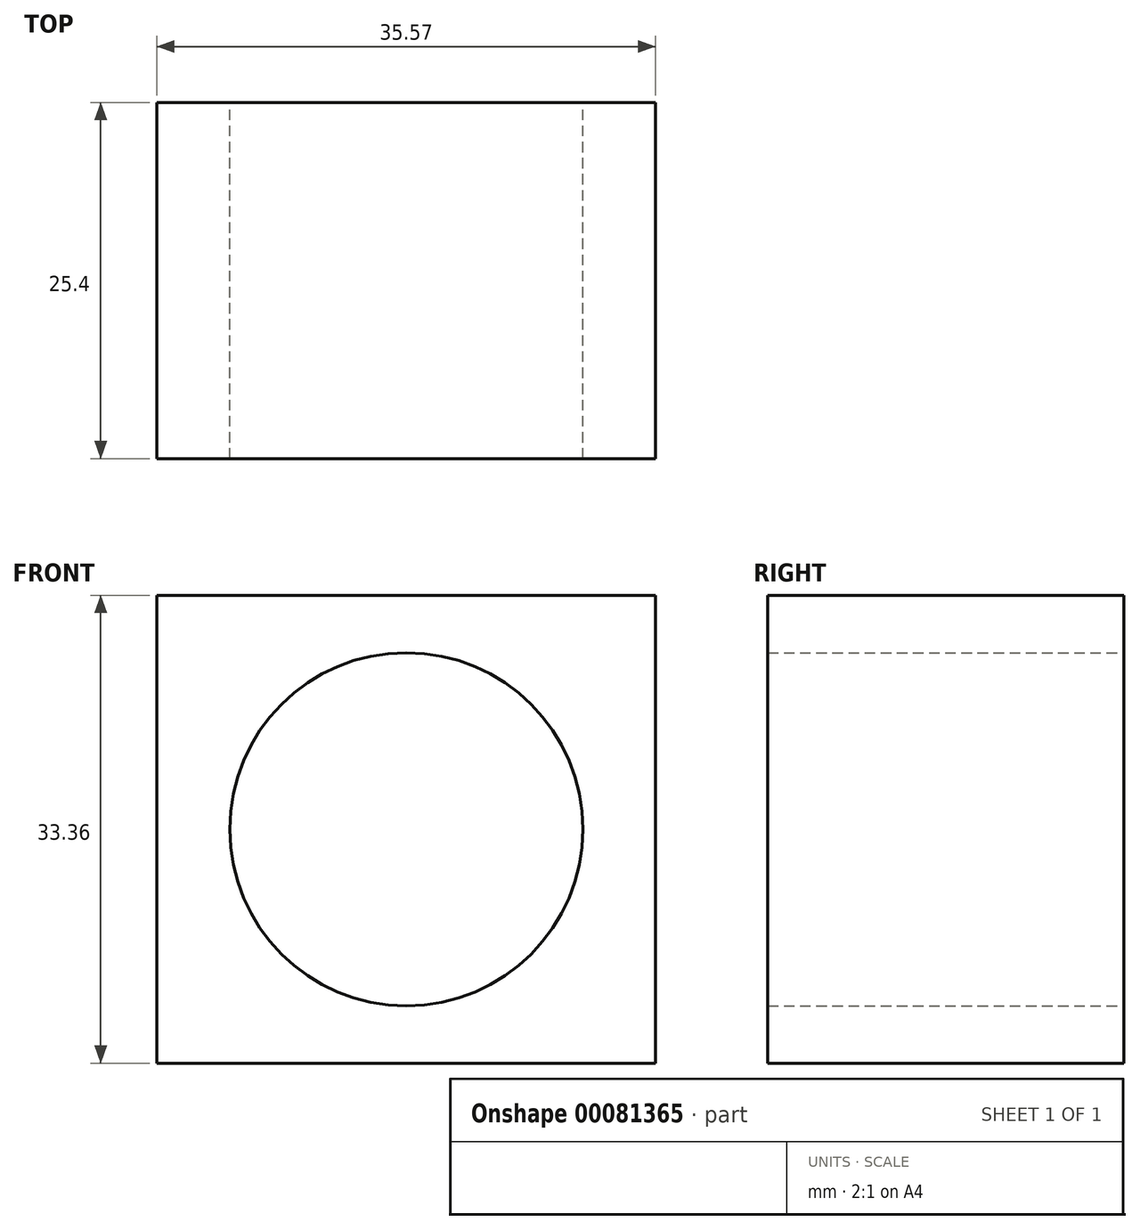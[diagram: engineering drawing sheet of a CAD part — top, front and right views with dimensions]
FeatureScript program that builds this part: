
annotation { "Feature Type Name" : "Feature", "Feature Type Description" : "" }
export const myFeature = defineFeature(function(context is Context, id is Id, definition is map)
    precondition{}
    {
        {
            var Q0;
            Q0=qCreatedBy(makeId("Front.planeOp"),FACE);
            var sketch = newSketch(context, id + "F0", { "sketchPlane" : qUnion([Q0])});
            skLineSegment(sketch, "E0.bottom", {"start": v(0, 0) * mm, "end": v(-35.57, 0) * mm});
            skLineSegment(sketch, "E0.top", {"start": v(0, 33.36) * mm, "end": v(-35.57, 33.36) * mm});
            skLineSegment(sketch, "E0.left", {"start": v(0, 0) * mm, "end": v(0, 33.36) * mm});
            skLineSegment(sketch, "E0.right", {"start": v(-35.57, 0) * mm, "end": v(-35.57, 33.36) * mm});
            skLineSegment(sketch, "E1", {"start": v(0, 0) * mm, "end": v(-35.57, 33.36) * mm});
            skLineSegment(sketch, "E2", {"start": v(-35.57, 0) * mm, "end": v(0, 33.36) * mm});
            skCircle(sketch, "E3", {"center": v(-17.78, 16.68) * mm, "radius": 12.6 * mm});
            skSolve(sketch);
        }
        {
            var Q0;
            Q0 = qSketchRegion(id + "F0", true);
            extrude(context, id + "F1", {"entities" : qUnion([Q0]), "depth" : 25.4 * mm});
        }
    });
